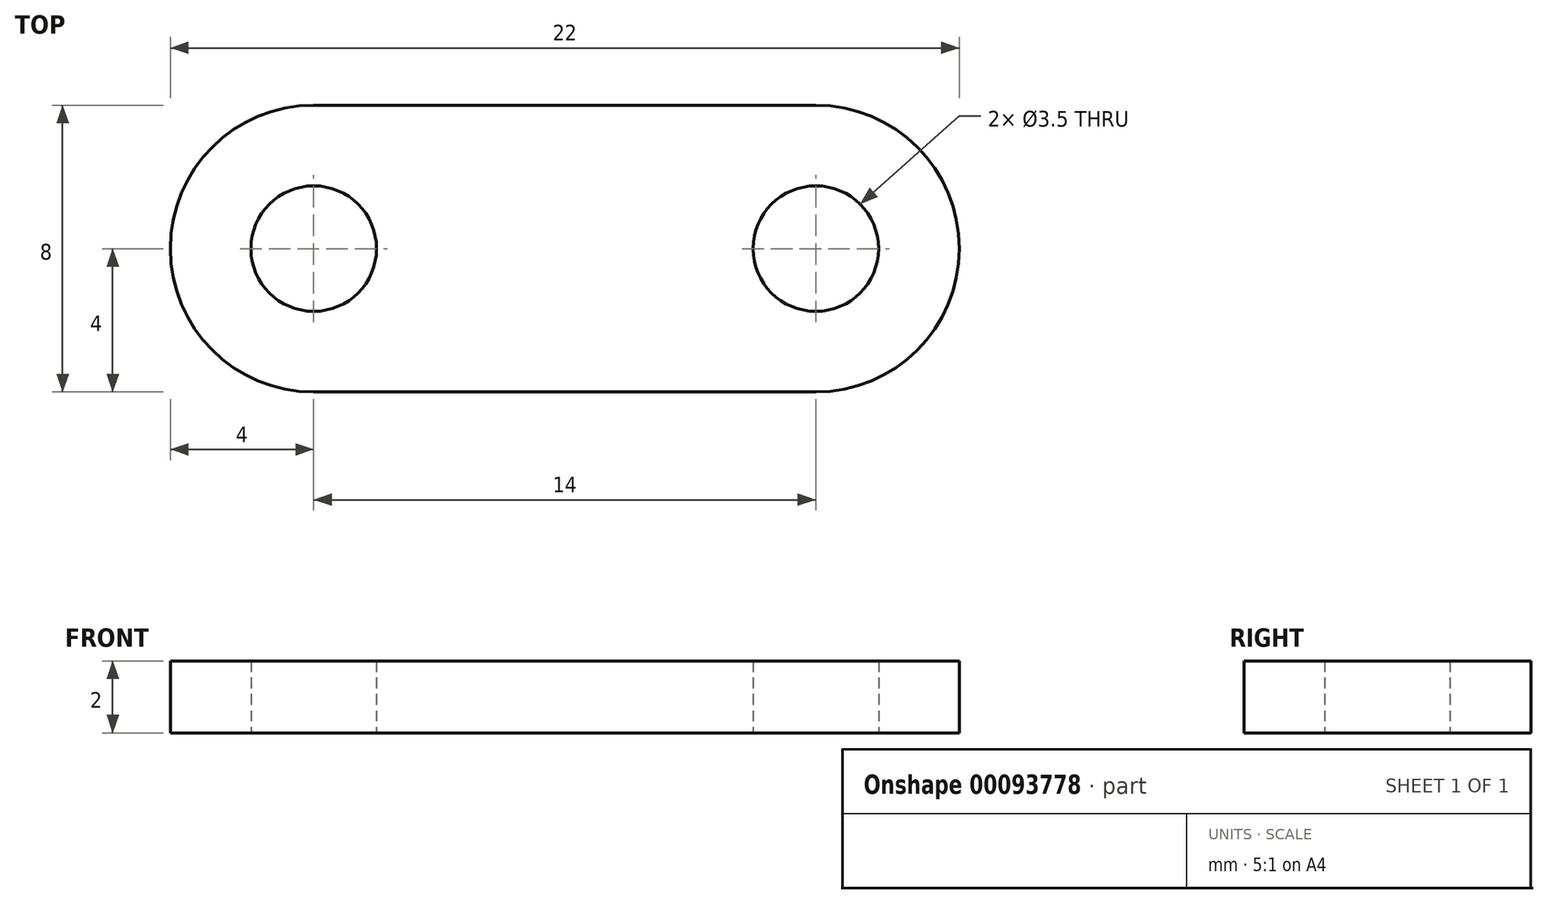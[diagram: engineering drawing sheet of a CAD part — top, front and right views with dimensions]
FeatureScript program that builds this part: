
annotation { "Feature Type Name" : "Feature", "Feature Type Description" : "" }
export const myFeature = defineFeature(function(context is Context, id is Id, definition is map)
    precondition{}
    {
        {
            var Q0;
            Q0=qCreatedBy(makeId("Top.planeOp"),FACE);
            var sketch = newSketch(context, id + "F0", { "sketchPlane" : qUnion([Q0])});
            skLineSegment(sketch, "E0.bottom", {"start": v(-7, 4) * mm, "end": v(7, 4) * mm});
            skLineSegment(sketch, "E0.top", {"start": v(-7, -4) * mm, "end": v(7, -4) * mm});
            skLineSegment(sketch, "E0.left", {"start": v(-11, 0) * mm, "end": v(-11, 0) * mm});
            skLineSegment(sketch, "E0.right", {"start": v(11, 0) * mm, "end": v(11, 0) * mm});
            skPoint(sketch, "E0.middle", {"position": v(0, 0) * mm});
            skPoint(sketch, "E1", {"position": v(-7, 0) * mm});
            skPoint(sketch, "E1.positionSnap0", {"position": v(-11, 0) * mm});
            skLineSegment(sketch, "E2", {"start": v(0, 4) * mm, "end": v(0, -4) * mm, "construction": true});
            skCircle(sketch, "E3", {"center": v(-7, 0) * mm, "radius": 1.75 * mm});
            skCircle(sketch, "E4.MirrorC", {"center": v(7, 0) * mm, "radius": 1.75 * mm});
            skPoint(sketch, "E5.visualSharp", {"position": v(-11, 4) * mm});
            skArc(sketch, "E5.filletArc", {"start": v(-7, 4) * mm, "mid": v(-9.83, 2.83) * mm, "end": v(-11, 0) * mm});
            skPoint(sketch, "E6.visualSharp", {"position": v(-11, -4) * mm});
            skArc(sketch, "E6.filletArc", {"start": v(-11, 0) * mm, "mid": v(-9.83, -2.83) * mm, "end": v(-7, -4) * mm});
            skPoint(sketch, "E7.visualSharp", {"position": v(11, 4) * mm});
            skArc(sketch, "E7.filletArc", {"start": v(11, 0) * mm, "mid": v(9.83, 2.83) * mm, "end": v(7, 4) * mm});
            skPoint(sketch, "E8.visualSharp", {"position": v(11, -4) * mm});
            skArc(sketch, "E8.filletArc", {"start": v(7, -4) * mm, "mid": v(9.83, -2.83) * mm, "end": v(11, 0) * mm});
            skSolve(sketch);
        }
        {
            var Q0;
            Q0=makeQuery(id+"F0.imprint","IMPRINT",FACE,{"disambiguationData":[TD([[makeQuery(id+"F0.imprint","IMPRINT",EDGE,{"derivedFrom":sQuery(id+"F0.wireOp",EDGE,"E0.bottom")}),-1.0]])]});
            extrude(context, id + "F1", {"entities" : qUnion([Q0]), "depth" : 2 * mm});
        }
    });
